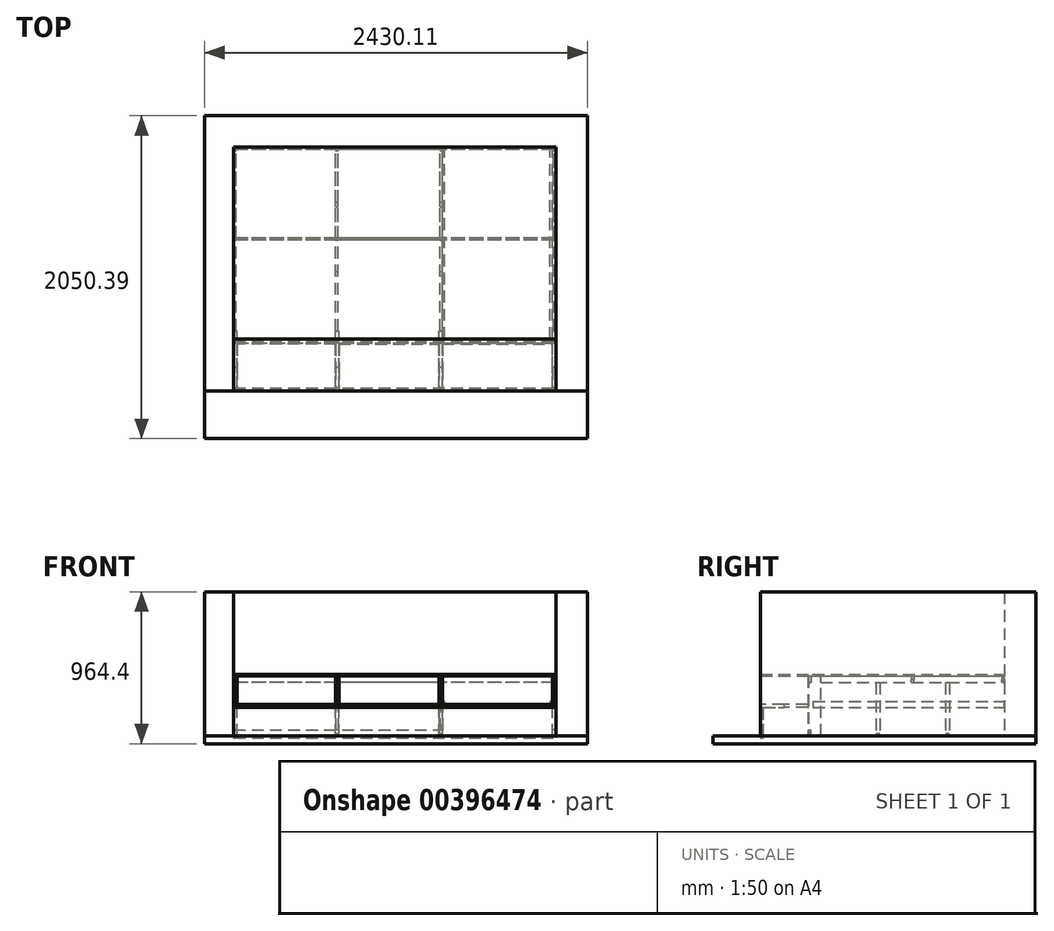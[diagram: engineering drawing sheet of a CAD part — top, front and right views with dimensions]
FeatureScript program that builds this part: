
annotation { "Feature Type Name" : "Feature", "Feature Type Description" : "" }
export const myFeature = defineFeature(function(context is Context, id is Id, definition is map)
    precondition{}
    {
        {
            var Q0;
            Q0=qCreatedBy(makeId("Top.planeOp"),FACE);
            cPlane(context, id + "F0", {"entities" : qUnion([Q0]), "cplaneType" : CPlaneType.OFFSET, "offset" : 180 * mm, "width" : 150 * mm, "height" : 150 * mm});
        }
        {
            var Q0;
            Q0=qCreatedBy(id+"F0.planeOp",FACE);
            var sketch = newSketch(context, id + "F1", { "sketchPlane" : qUnion([Q0])});
            skLineSegment(sketch, "E0.bottom", {"start": v(0, 0) * mm, "end": v(-2045, 0) * mm});
            skLineSegment(sketch, "E0.top", {"start": v(-20, 300) * mm, "end": v(-720, 300) * mm});
            skLineSegment(sketch, "E0.left", {"start": v(0, 0) * mm, "end": v(0, 150) * mm});
            skLineSegment(sketch, "E0.right", {"start": v(-2045, 0) * mm, "end": v(-2045, 150) * mm});
            skLineSegment(sketch, "E1.top", {"start": v(-2045, 150) * mm, "end": v(-2025, 150) * mm});
            skLineSegment(sketch, "E1.right", {"start": v(-2025, 300) * mm, "end": v(-2025, 150) * mm});
            skLineSegment(sketch, "E2.top", {"start": v(-1377.5, 150) * mm, "end": v(-1397.5, 150) * mm});
            skLineSegment(sketch, "E2.left", {"start": v(-1377.5, 300) * mm, "end": v(-1377.5, 150) * mm});
            skLineSegment(sketch, "E2.right", {"start": v(-1397.5, 300) * mm, "end": v(-1397.5, 150) * mm});
            skLineSegment(sketch, "E3.top", {"start": v(-720, 150) * mm, "end": v(-740, 150) * mm});
            skLineSegment(sketch, "E3.left", {"start": v(-720, 300) * mm, "end": v(-720, 150) * mm});
            skLineSegment(sketch, "E3.right", {"start": v(-740, 300) * mm, "end": v(-740, 150) * mm});
            skLineSegment(sketch, "E4.top", {"start": v(0, 150) * mm, "end": v(-20, 150) * mm});
            skLineSegment(sketch, "E5.trimOffspring", {"start": v(-1397.5, 300) * mm, "end": v(-2025, 300) * mm});
            skLineSegment(sketch, "E6.trimOffspring", {"start": v(-740, 300) * mm, "end": v(-1377.5, 300) * mm});
            skLineSegment(sketch, "E7", {"start": v(-20, 150) * mm, "end": v(-20, 300) * mm});
            skSolve(sketch);
        }
        {
            var Q0;
            Q0=makeQuery(id+"F1.imprint","IMPRINT",FACE,{"disambiguationData":[TD([[makeQuery(id+"F1.imprint","IMPRINT",EDGE,{"derivedFrom":sQuery(id+"F1.wireOp",EDGE,"E0.bottom")}),-1.0]])]});
            extrude(context, id + "F2", {"entities" : qUnion([Q0]), "depth" : 20 * mm});
        }
        {
            var Q0;
            Q0=makeQuery(id+"F2.opExtrude","SWEPT_FACE",FACE,{"disambiguationData":[OSD([sQuery(id+"F1.wireOp",EDGE,"E7")])]});
            var sketch = newSketch(context, id + "F3", { "sketchPlane" : qUnion([Q0])});
            skLineSegment(sketch, "E8.bottom", {"start": v(20, 0) * mm, "end": v(305, 0) * mm});
            skLineSegment(sketch, "E8.top", {"start": v(0, 380) * mm, "end": v(305, 380) * mm});
            skLineSegment(sketch, "E8.right", {"start": v(383.3, 0) * mm, "end": v(383.3, 380) * mm});
            skLineSegment(sketch, "E9.0.0", {"start": v(20, 180) * mm, "end": v(150, 180) * mm});
            skLineSegment(sketch, "E9.0.1", {"start": v(150, 180) * mm, "end": v(150, 200) * mm});
            skLineSegment(sketch, "E9.0.2", {"start": v(150, 200) * mm, "end": v(0, 200) * mm});
            skLineSegment(sketch, "E10.trimOffspring", {"start": v(0, 200) * mm, "end": v(0, 380) * mm});
            skLineSegment(sketch, "E11.top", {"start": v(305, 340) * mm, "end": v(320, 340) * mm});
            skLineSegment(sketch, "E11.left", {"start": v(305, 380) * mm, "end": v(305, 340) * mm});
            skLineSegment(sketch, "E11.right", {"start": v(320, 380) * mm, "end": v(320, 340) * mm});
            skLineSegment(sketch, "E12.top", {"start": v(305, 40) * mm, "end": v(320, 40) * mm});
            skLineSegment(sketch, "E12.left", {"start": v(305, 0) * mm, "end": v(305, 40) * mm});
            skLineSegment(sketch, "E12.right", {"start": v(320, 0) * mm, "end": v(320, 40) * mm});
            skLineSegment(sketch, "E13.0", {"start": v(20, 0) * mm, "end": v(20, 180) * mm});
            skPoint(sketch, "E14.orphan", {"position": v(0, 180) * mm});
            skLineSegment(sketch, "E15.trimOffspring", {"start": v(320, 380) * mm, "end": v(383.3, 380) * mm});
            skLineSegment(sketch, "E16.trimOffspring", {"start": v(320, 0) * mm, "end": v(383.3, 0) * mm});
            skSolve(sketch);
        }
        {
            var Q0;
            Q0=makeQuery(id+"F3.imprint","IMPRINT",FACE,{"disambiguationData":[TD([[makeQuery(id+"F3.imprint","IMPRINT",EDGE,{"derivedFrom":sQuery(id+"F3.wireOp",EDGE,"E8.bottom")}),1.0]])]});
            var Q1;
            Q1=makeQuery(id+"F3.imprint","IMPRINT",FACE,{"disambiguationData":[TD([[makeQuery(id+"F3.imprint","IMPRINT",EDGE,{"derivedFrom":sQuery(id+"F3.wireOp",EDGE,"E9.0.1")}),1.0]])]});
            extrude(context, id + "F4", {"entities" : qUnion([Q0, Q1]), "depth" : 20 * mm});
        }
        {
            var Q0;
            Q0=makeQuery(id+"F4.opExtrude","SWEPT_BODY",BODY,{"disambiguationData":[OSD([sQuery(id+"F3.wireOp",EDGE,"E8.bottom"),sQuery(id+"F3.wireOp",EDGE,"E8.top"),sQuery(id+"F3.wireOp",EDGE,"E8.left"),sQuery(id+"F3.wireOp",EDGE,"E8.right"),sQuery(id+"F3.wireOp",EDGE,"E9.0.0"),sQuery(id+"F3.wireOp",EDGE,"E9.0.1"),sQuery(id+"F3.wireOp",EDGE,"E9.0.2"),sQuery(id+"F3.wireOp",EDGE,"E10.trimOffspring")])]});
            transform(context, id + "F5", {"entities" : qUnion([Q0]), "transformType" : TransformType.TRANSLATION_3D, "dx" : -720 * mm, "dy" : 0 * mm, "dz" : 0 * mm, "makeCopy" : true});
        }
        {
            var Q0;
            Q0=makeQuery(id+"F5.opPattern","COPY",BODY,{"derivedFrom":makeQuery(id+"F4.opExtrude","SWEPT_BODY",BODY,{"disambiguationData":[OSD([sQuery(id+"F3.wireOp",EDGE,"E8.bottom"),sQuery(id+"F3.wireOp",EDGE,"E8.top"),sQuery(id+"F3.wireOp",EDGE,"E8.left"),sQuery(id+"F3.wireOp",EDGE,"E8.right"),sQuery(id+"F3.wireOp",EDGE,"E9.0.0"),sQuery(id+"F3.wireOp",EDGE,"E9.0.1"),sQuery(id+"F3.wireOp",EDGE,"E9.0.2"),sQuery(id+"F3.wireOp",EDGE,"E10.trimOffspring")])]}),"instanceName":"1"});
            transform(context, id + "F6", {"entities" : qUnion([Q0]), "transformType" : TransformType.TRANSLATION_3D, "dx" : -657.5 * mm, "dy" : 0 * mm, "dz" : 0 * mm, "makeCopy" : true});
        }
        {
            var Q0;
            Q0=makeQuery(id+"F6.opPattern","COPY",BODY,{"derivedFrom":makeQuery(id+"F5.opPattern","COPY",BODY,{"derivedFrom":makeQuery(id+"F4.opExtrude","SWEPT_BODY",BODY,{"disambiguationData":[OSD([sQuery(id+"F3.wireOp",EDGE,"E8.bottom"),sQuery(id+"F3.wireOp",EDGE,"E8.top"),sQuery(id+"F3.wireOp",EDGE,"E8.left"),sQuery(id+"F3.wireOp",EDGE,"E8.right"),sQuery(id+"F3.wireOp",EDGE,"E9.0.0"),sQuery(id+"F3.wireOp",EDGE,"E9.0.1"),sQuery(id+"F3.wireOp",EDGE,"E9.0.2"),sQuery(id+"F3.wireOp",EDGE,"E10.trimOffspring")])]}),"instanceName":"1"}),"instanceName":"1"});
            transform(context, id + "F7", {"entities" : qUnion([Q0]), "transformType" : TransformType.TRANSLATION_3D, "dx" : -647.5 * mm, "dy" : 0 * mm, "dz" : 0 * mm, "makeCopy" : true});
        }
        {
            var Q0;
            Q0=qCreatedBy(makeId("Top.planeOp"),FACE);
            var sketch = newSketch(context, id + "F8", { "sketchPlane" : qUnion([Q0])});
            skPoint(sketch, "E17.0", {"position": v(-2045, 320) * mm});
            skPoint(sketch, "E18.0", {"position": v(-720, 305) * mm});
            skLineSegment(sketch, "E19.bottom", {"start": v(-2045, 320) * mm, "end": v(-720, 320) * mm});
            skLineSegment(sketch, "E19.top", {"start": v(-2045, 305) * mm, "end": v(-720, 305) * mm});
            skLineSegment(sketch, "E19.right", {"start": v(-720, 320) * mm, "end": v(-720, 305) * mm});
            skLineSegment(sketch, "E20", {"start": v(-2045, 320) * mm, "end": v(-2045, 305) * mm});
            skSolve(sketch);
        }
        {
            var Q0;
            Q0 = qSketchRegion(id + "F8", true);
            extrude(context, id + "F9", {"entities" : qUnion([Q0]), "depth" : 40 * mm});
        }
        {
            var Q0;
            Q0=makeQuery(id+"F4.opExtrude","CAP_FACE",FACE,{"disambiguationData":[OSD([sQuery(id+"F3.wireOp",EDGE,"E8.bottom"),sQuery(id+"F3.wireOp",EDGE,"E8.top"),sQuery(id+"F3.wireOp",EDGE,"E8.left"),sQuery(id+"F3.wireOp",EDGE,"E8.right"),sQuery(id+"F3.wireOp",EDGE,"E9.0.0"),sQuery(id+"F3.wireOp",EDGE,"E9.0.1"),sQuery(id+"F3.wireOp",EDGE,"E9.0.2"),sQuery(id+"F3.wireOp",EDGE,"E10.trimOffspring"),sQuery(id+"F3.wireOp",EDGE,"E11.top"),sQuery(id+"F3.wireOp",EDGE,"E11.left"),sQuery(id+"F3.wireOp",EDGE,"E11.right"),sQuery(id+"F3.wireOp",EDGE,"E12.top"),sQuery(id+"F3.wireOp",EDGE,"E12.left"),sQuery(id+"F3.wireOp",EDGE,"E12.right")])],"isStart":false});
            var sketch = newSketch(context, id + "F10", { "sketchPlane" : qUnion([Q0])});
            skLineSegment(sketch, "E21.bottom", {"start": v(383.3, 380) * mm, "end": v(959.15, 380) * mm});
            skLineSegment(sketch, "E21.top", {"start": v(383.3, 340) * mm, "end": v(1530, 340) * mm});
            skLineSegment(sketch, "E21.right", {"start": v(1550, 380) * mm, "end": v(1550, 360) * mm});
            skLineSegment(sketch, "E22.0", {"start": v(974.15, 380) * mm, "end": v(974.15, 360) * mm});
            skLineSegment(sketch, "E23.0", {"start": v(959.15, 380) * mm, "end": v(959.15, 360) * mm});
            skLineSegment(sketch, "E24.trimOffspring", {"start": v(974.15, 380) * mm, "end": v(1550, 380) * mm});
            skLineSegment(sketch, "E25", {"start": v(974.15, 360) * mm, "end": v(959.15, 360) * mm});
            skLineSegment(sketch, "E26", {"start": v(1550, 360) * mm, "end": v(1530, 360) * mm});
            skLineSegment(sketch, "E27", {"start": v(1530, 360) * mm, "end": v(1530, 340) * mm});
            skLineSegment(sketch, "E28", {"start": v(383.3, 380) * mm, "end": v(383.3, 340) * mm});
            skSolve(sketch);
        }
        {
            var Q0;
            Q0 = qSketchRegion(id + "F10", true);
            extrude(context, id + "F11", {"entities" : qUnion([Q0]), "oppositeDirection" : true, "depth" : 15 * mm});
        }
        {
            var Q0;
            Q0=makeQuery(id+"F11.opExtrude","SWEPT_BODY",BODY,{"disambiguationData":[OSD([sQuery(id+"F10.wireOp",EDGE,"E21.bottom"),sQuery(id+"F10.wireOp",EDGE,"E21.top"),sQuery(id+"F10.wireOp",EDGE,"E21.left"),sQuery(id+"F10.wireOp",EDGE,"E21.right"),sQuery(id+"F10.wireOp",EDGE,"E22.0"),sQuery(id+"F10.wireOp",EDGE,"E23.0"),sQuery(id+"F10.wireOp",EDGE,"E24.trimOffspring"),sQuery(id+"F10.wireOp",EDGE,"E25"),sQuery(id+"F10.wireOp",EDGE,"E26"),sQuery(id+"F10.wireOp",EDGE,"sHKAyeEh-goYe-EqED-aYtI-0ct1l86yUGji")])]});
            transform(context, id + "F12", {"entities" : qUnion([Q0]), "transformType" : TransformType.TRANSLATION_3D, "dx" : -2030 * mm, "dy" : 0 * mm, "dz" : 0 * mm, "makeCopy" : true});
        }
        {
            var Q0;
            Q0=makeQuery(id+"F11.opExtrude","SWEPT_BODY",BODY,{"disambiguationData":[OSD([sQuery(id+"F10.wireOp",EDGE,"E21.bottom"),sQuery(id+"F10.wireOp",EDGE,"E21.top"),sQuery(id+"F10.wireOp",EDGE,"E21.left"),sQuery(id+"F10.wireOp",EDGE,"E21.right"),sQuery(id+"F10.wireOp",EDGE,"E22.0"),sQuery(id+"F10.wireOp",EDGE,"E23.0"),sQuery(id+"F10.wireOp",EDGE,"E24.trimOffspring"),sQuery(id+"F10.wireOp",EDGE,"E25"),sQuery(id+"F10.wireOp",EDGE,"E26"),sQuery(id+"F10.wireOp",EDGE,"sHKAyeEh-goYe-EqED-aYtI-0ct1l86yUGji")])]});
            transform(context, id + "F13", {"entities" : qUnion([Q0]), "transformType" : TransformType.TRANSLATION_3D, "dx" : -720 * mm, "dy" : 0 * mm, "dz" : 0 * mm, "makeCopy" : true});
        }
        {
            var Q0;
            Q0=makeQuery(id+"F13.opPattern","COPY",BODY,{"derivedFrom":makeQuery(id+"F11.opExtrude","SWEPT_BODY",BODY,{"disambiguationData":[OSD([sQuery(id+"F10.wireOp",EDGE,"E21.bottom"),sQuery(id+"F10.wireOp",EDGE,"E21.top"),sQuery(id+"F10.wireOp",EDGE,"E21.left"),sQuery(id+"F10.wireOp",EDGE,"E21.right"),sQuery(id+"F10.wireOp",EDGE,"E22.0"),sQuery(id+"F10.wireOp",EDGE,"E23.0"),sQuery(id+"F10.wireOp",EDGE,"E24.trimOffspring"),sQuery(id+"F10.wireOp",EDGE,"E25"),sQuery(id+"F10.wireOp",EDGE,"E26"),sQuery(id+"F10.wireOp",EDGE,"sHKAyeEh-goYe-EqED-aYtI-0ct1l86yUGji")])]}),"instanceName":"1"});
            transform(context, id + "F14", {"entities" : qUnion([Q0]), "transformType" : TransformType.TRANSLATION_3D, "dx" : -662.5 * mm, "dy" : 0 * mm, "dz" : 0 * mm, "makeCopy" : true});
        }
        {
            var Q0;
            Q0=makeQuery(id+"F11.opExtrude","SWEPT_FACE",FACE,{"disambiguationData":[OSD([sQuery(id+"F10.wireOp",EDGE,"E21.right")])]});
            var sketch = newSketch(context, id + "F15", { "sketchPlane" : qUnion([Q0])});
            skLineSegment(sketch, "E29.bottom", {"start": v(15, 380) * mm, "end": v(720, 380) * mm});
            skLineSegment(sketch, "E29.top", {"start": v(0, 340) * mm, "end": v(2045, 340) * mm});
            skLineSegment(sketch, "E29.left", {"start": v(0, 360) * mm, "end": v(0, 340) * mm});
            skLineSegment(sketch, "E30", {"start": v(2045, 340) * mm, "end": v(2045, 360) * mm});
            skPoint(sketch, "E31.0", {"position": v(2030, 360) * mm});
            skLineSegment(sketch, "E32", {"start": v(2045, 360) * mm, "end": v(2030, 360) * mm});
            skLineSegment(sketch, "E33", {"start": v(2030, 360) * mm, "end": v(2030, 380) * mm});
            skPoint(sketch, "E34.orphan", {"position": v(2045, 380) * mm});
            skPoint(sketch, "E35.0", {"position": v(1397.5, 360) * mm});
            skPoint(sketch, "E36.0", {"position": v(1382.5, 360) * mm});
            skLineSegment(sketch, "E37", {"start": v(1382.5, 380) * mm, "end": v(1382.5, 360) * mm});
            skLineSegment(sketch, "E38", {"start": v(1397.5, 360) * mm, "end": v(1397.5, 380) * mm});
            skLineSegment(sketch, "E39.trimOffspring", {"start": v(1397.5, 380) * mm, "end": v(2030, 380) * mm});
            skLineSegment(sketch, "E40", {"start": v(1382.5, 360) * mm, "end": v(1397.5, 360) * mm});
            skPoint(sketch, "E41.0", {"position": v(735, 360) * mm});
            skPoint(sketch, "E42.0", {"position": v(720, 380) * mm});
            skLineSegment(sketch, "E43.bottom", {"start": v(735, 360) * mm, "end": v(720, 360) * mm});
            skLineSegment(sketch, "E43.left", {"start": v(735, 360) * mm, "end": v(735, 380) * mm});
            skLineSegment(sketch, "E43.right", {"start": v(720, 360) * mm, "end": v(720, 380) * mm});
            skLineSegment(sketch, "E44.trimOffspring", {"start": v(735, 380) * mm, "end": v(1382.5, 380) * mm});
            skPoint(sketch, "E45.0", {"position": v(15, 360) * mm});
            skLineSegment(sketch, "E46.bottom", {"start": v(15, 360) * mm, "end": v(0, 360) * mm});
            skLineSegment(sketch, "E46.left", {"start": v(15, 360) * mm, "end": v(15, 380) * mm});
            skPoint(sketch, "E46.top.end.orphan", {"position": v(0, 380) * mm});
            skSolve(sketch);
        }
        {
            var Q0;
            Q0=makeQuery(id+"F15.imprint","IMPRINT",FACE,{"disambiguationData":[TD([[makeQuery(id+"F15.imprint","IMPRINT",EDGE,{"derivedFrom":sQuery(id+"F15.wireOp",EDGE,"E29.bottom")}),-1.0]])]});
            extrude(context, id + "F16", {"entities" : qUnion([Q0]), "oppositeDirection" : true, "depth" : 15 * mm});
        }
        {
            var Q0;
            Q0=makeQuery(id+"F13.opPattern","COPY",FACE,{"derivedFrom":makeQuery(id+"F11.opExtrude","CAP_FACE",FACE,{"disambiguationData":[OSD([sQuery(id+"F10.wireOp",EDGE,"E21.bottom"),sQuery(id+"F10.wireOp",EDGE,"E21.top"),sQuery(id+"F10.wireOp",EDGE,"E21.left"),sQuery(id+"F10.wireOp",EDGE,"E21.right"),sQuery(id+"F10.wireOp",EDGE,"E22.0"),sQuery(id+"F10.wireOp",EDGE,"E23.0"),sQuery(id+"F10.wireOp",EDGE,"E24.trimOffspring"),sQuery(id+"F10.wireOp",EDGE,"E25"),sQuery(id+"F10.wireOp",EDGE,"E26"),sQuery(id+"F10.wireOp",EDGE,"E27")])],"isStart":true}),"instanceName":"1"});
            var sketch = newSketch(context, id + "F17", { "sketchPlane" : qUnion([Q0])});
            skLineSegment(sketch, "E47.0", {"start": v(733.3, 340) * mm, "end": v(733.3, 15) * mm});
            skLineSegment(sketch, "E48.0", {"start": v(760, 340) * mm, "end": v(760, 15) * mm});
            skLineSegment(sketch, "E49", {"start": v(733.3, 340) * mm, "end": v(760, 340) * mm});
            skLineSegment(sketch, "E50", {"start": v(733.3, 15) * mm, "end": v(760, 15) * mm});
            skPoint(sketch, "E51.0", {"position": v(20, 0) * mm});
            skSolve(sketch);
        }
        {
            var Q0;
            Q0=makeQuery(id+"F17.imprint","IMPRINT",FACE,{"disambiguationData":[TD([[makeQuery(id+"F17.imprint","IMPRINT",EDGE,{"derivedFrom":sQuery(id+"F17.wireOp",EDGE,"E47.0")}),1.0]])]});
            extrude(context, id + "F18", {"entities" : qUnion([Q0]), "oppositeDirection" : true, "depth" : 15 * mm});
        }
        {
            var Q0;
            Q0=makeQuery(id+"F18.opExtrude","SWEPT_BODY",BODY,{"disambiguationData":[OSD([sQuery(id+"F17.wireOp",EDGE,"E47.0"),sQuery(id+"F17.wireOp",EDGE,"E48.0"),sQuery(id+"F17.wireOp",EDGE,"E49"),sQuery(id+"F17.wireOp",EDGE,"E50")])]});
            transform(context, id + "F19", {"entities" : qUnion([Q0]), "transformType" : TransformType.TRANSLATION_3D, "dx" : 0 * mm, "dy" : 440 * mm, "dz" : 0 * mm, "makeCopy" : true});
        }
        {
            var Q0;
            Q0=makeQuery(id+"F18.opExtrude","SWEPT_BODY",BODY,{"disambiguationData":[OSD([sQuery(id+"F17.wireOp",EDGE,"E47.0"),sQuery(id+"F17.wireOp",EDGE,"E48.0"),sQuery(id+"F17.wireOp",EDGE,"E49"),sQuery(id+"F17.wireOp",EDGE,"E50")])]});
            transform(context, id + "F20", {"entities" : qUnion([Q0]), "transformType" : TransformType.TRANSLATION_3D, "dx" : -662.5 * mm, "dy" : 0 * mm, "dz" : 0 * mm, "makeCopy" : true});
        }
        {
            var Q0;
            Q0=makeQuery(id+"F19.opPattern","COPY",BODY,{"derivedFrom":makeQuery(id+"F18.opExtrude","SWEPT_BODY",BODY,{"disambiguationData":[OSD([sQuery(id+"F17.wireOp",EDGE,"E47.0"),sQuery(id+"F17.wireOp",EDGE,"E48.0"),sQuery(id+"F17.wireOp",EDGE,"E49"),sQuery(id+"F17.wireOp",EDGE,"E50")])]}),"instanceName":"1"});
            transform(context, id + "F21", {"entities" : qUnion([Q0]), "transformType" : TransformType.TRANSLATION_3D, "dx" : -662.5 * mm, "dy" : 0 * mm, "dz" : 0 * mm, "makeCopy" : true});
        }
        {
            var Q0;
            Q0=makeQuery(id+"F5.opPattern","COPY",FACE,{"derivedFrom":makeQuery(id+"F4.opExtrude","CAP_FACE",FACE,{"disambiguationData":[OSD([sQuery(id+"F3.wireOp",EDGE,"E8.bottom"),sQuery(id+"F3.wireOp",EDGE,"E8.top"),sQuery(id+"F3.wireOp",EDGE,"E8.left"),sQuery(id+"F3.wireOp",EDGE,"E8.right"),sQuery(id+"F3.wireOp",EDGE,"E9.0.0"),sQuery(id+"F3.wireOp",EDGE,"E9.0.1"),sQuery(id+"F3.wireOp",EDGE,"E9.0.2"),sQuery(id+"F3.wireOp",EDGE,"E10.trimOffspring"),sQuery(id+"F3.wireOp",EDGE,"E11.top"),sQuery(id+"F3.wireOp",EDGE,"E11.left"),sQuery(id+"F3.wireOp",EDGE,"E11.right"),sQuery(id+"F3.wireOp",EDGE,"E12.top"),sQuery(id+"F3.wireOp",EDGE,"E12.left"),sQuery(id+"F3.wireOp",EDGE,"E12.right")])],"isStart":false}),"instanceName":"1"});
            var sketch = newSketch(context, id + "F22", { "sketchPlane" : qUnion([Q0])});
            skPoint(sketch, "E52.0", {"position": v(1550, 340) * mm});
            skLineSegment(sketch, "E53.bottom", {"start": v(333.3, 180) * mm, "end": v(1550, 180) * mm});
            skLineSegment(sketch, "E53.top", {"start": v(333.3, 220) * mm, "end": v(1550, 220) * mm});
            skLineSegment(sketch, "E53.right", {"start": v(1550, 180) * mm, "end": v(1550, 220) * mm});
            skLineSegment(sketch, "E54", {"start": v(333.3, 220) * mm, "end": v(333.3, 180) * mm});
            skSolve(sketch);
        }
        {
            var Q0;
            Q0=makeQuery(id+"F22.imprint","IMPRINT",FACE,{"disambiguationData":[TD([[makeQuery(id+"F22.imprint","IMPRINT",EDGE,{"derivedFrom":sQuery(id+"F22.wireOp",EDGE,"E53.bottom")}),1.0]])]});
            extrude(context, id + "F23", {"entities" : qUnion([Q0]), "depth" : 15 * mm});
        }
        {
            var Q0;
            Q0=makeQuery(id+"F23.opExtrude","SWEPT_BODY",BODY,{"disambiguationData":[OSD([sQuery(id+"F22.wireOp",EDGE,"E53.bottom"),sQuery(id+"F22.wireOp",EDGE,"E53.top"),sQuery(id+"F22.wireOp",EDGE,"E53.right"),sQuery(id+"F22.wireOp",EDGE,"E54")])]});
            transform(context, id + "F24", {"entities" : qUnion([Q0]), "transformType" : TransformType.TRANSLATION_3D, "dx" : (700 - 15) * mm, "dy" : 0 * mm, "dz" : 0 * mm, "makeCopy" : true});
        }
        {
            var Q0;
            Q0=qCreatedBy(makeId("Top.planeOp"),FACE);
            var sketch = newSketch(context, id + "F25", { "sketchPlane" : qUnion([Q0])});
            skPoint(sketch, "E55.0", {"position": v(0, 1550) * mm});
            skPoint(sketch, "E56.0", {"position": v(-2045, 1550) * mm});
            skPoint(sketch, "E57.0", {"position": v(-2045, 0) * mm});
            skLineSegment(sketch, "E58.bottom", {"start": v(0, 0) * mm, "end": v(200, 0) * mm});
            skLineSegment(sketch, "E58.left", {"start": v(0, 0) * mm, "end": v(0, 1550) * mm});
            skLineSegment(sketch, "E58.right", {"start": v(200, 0) * mm, "end": v(200, 1750) * mm});
            skLineSegment(sketch, "E59.bottom", {"start": v(0, 1550) * mm, "end": v(-2045, 1550) * mm});
            skLineSegment(sketch, "E59.top", {"start": v(200, 1750) * mm, "end": v(-2230.11, 1750) * mm});
            skLineSegment(sketch, "E60.bottom", {"start": v(-2045, 0) * mm, "end": v(-2230.11, 0) * mm});
            skLineSegment(sketch, "E60.left", {"start": v(-2045, 0) * mm, "end": v(-2045, 1550) * mm});
            skLineSegment(sketch, "E60.right", {"start": v(-2230.11, 0) * mm, "end": v(-2230.11, 1750) * mm});
            skLineSegment(sketch, "E61.bottom", {"start": v(-2230.11, 0) * mm, "end": v(200, 0) * mm});
            skLineSegment(sketch, "E61.top", {"start": v(-2230.11, -300.39) * mm, "end": v(200, -300.39) * mm});
            skLineSegment(sketch, "E61.left", {"start": v(-2230.11, 0) * mm, "end": v(-2230.11, -300.39) * mm});
            skLineSegment(sketch, "E61.right", {"start": v(200, 0) * mm, "end": v(200, -300.39) * mm});
            skSolve(sketch);
        }
        {
            var Q0;
            {var subQ1=sQuery(id+"F25.wireOp",EDGE,"E58.left");Q0=makeQuery(id+"F25.imprint","IMPRINT",FACE,{"disambiguationData":[TD([[makeQuery(id+"F25.imprint","IMPRINT",EDGE,{"derivedFrom":subQ1}),-1.0]])]});}
            extrude(context, id + "F26", {"entities" : qUnion([Q0]), "depth" : 914.4 * mm});
        }
        {
            var Q0;
            Q0=makeQuery(id+"F25.imprint","IMPRINT",FACE,{"disambiguationData":[TD([[makeQuery(id+"F25.imprint","IMPRINT",EDGE,{"derivedFrom":sQuery(id+"F25.wireOp",EDGE,"E61.top")}),1.0]])]});
            var Q1;
            {var subQ0=sQuery(id+"F25.wireOp",EDGE,"E58.left");Q1=makeQuery(id+"F25.imprint","IMPRINT",FACE,{"disambiguationData":[TD([[makeQuery(id+"F25.imprint","IMPRINT",EDGE,{"derivedFrom":subQ0}),1.0]])]});}
            var Q2;
            {var subQ1=sQuery(id+"F25.wireOp",EDGE,"E58.left");Q2=makeQuery(id+"F25.imprint","IMPRINT",FACE,{"disambiguationData":[TD([[makeQuery(id+"F25.imprint","IMPRINT",EDGE,{"derivedFrom":subQ1}),-1.0]])]});}
            extrude(context, id + "F27", {"entities" : qUnion([Q0, Q1, Q2]), "oppositeDirection" : true, "depth" : 50 * mm});
        }
        {
            var Q0;
            Q0=makeQuery(id+"F4.opExtrude","CAP_FACE",FACE,{"disambiguationData":[OSD([sQuery(id+"F3.wireOp",EDGE,"E8.bottom"),sQuery(id+"F3.wireOp",EDGE,"E8.top"),sQuery(id+"F3.wireOp",EDGE,"E8.right"),sQuery(id+"F3.wireOp",EDGE,"E9.0.0"),sQuery(id+"F3.wireOp",EDGE,"E9.0.1"),sQuery(id+"F3.wireOp",EDGE,"E9.0.2"),sQuery(id+"F3.wireOp",EDGE,"E10.trimOffspring"),sQuery(id+"F3.wireOp",EDGE,"E11.top"),sQuery(id+"F3.wireOp",EDGE,"E11.left"),sQuery(id+"F3.wireOp",EDGE,"E11.right"),sQuery(id+"F3.wireOp",EDGE,"E12.top"),sQuery(id+"F3.wireOp",EDGE,"E12.left"),sQuery(id+"F3.wireOp",EDGE,"E12.right"),sQuery(id+"F3.wireOp",EDGE,"E13.0"),sQuery(id+"F3.wireOp",EDGE,"E15.trimOffspring"),sQuery(id+"F3.wireOp",EDGE,"E16.trimOffspring")])],"isStart":false});
            var sketch = newSketch(context, id + "F28", { "sketchPlane" : qUnion([Q0])});
            skLineSegment(sketch, "E62.bottom", {"start": v(305, 380) * mm, "end": v(320, 380) * mm});
            skLineSegment(sketch, "E62.top", {"start": v(305, 340) * mm, "end": v(320, 340) * mm});
            skLineSegment(sketch, "E62.left", {"start": v(305, 380) * mm, "end": v(305, 340) * mm});
            skLineSegment(sketch, "E62.right", {"start": v(320, 380) * mm, "end": v(320, 340) * mm});
            skSolve(sketch);
        }
        {
            var Q0;
            Q0 = qSketchRegion(id + "F28", true);
            extrude(context, id + "F29", {"entities" : qUnion([Q0]), "oppositeDirection" : true, "depth" : 2045 * mm});
        }
        {
            var Q0;
            Q0=makeQuery(id+"F29.opExtrude","SWEPT_FACE",FACE,{"disambiguationData":[OSD([sQuery(id+"F28.wireOp",EDGE,"E62.left")])]});
            var sketch = newSketch(context, id + "F30", { "sketchPlane" : qUnion([Q0])});
            skPoint(sketch, "E63.0", {"position": v(-2025, 380) * mm});
            skPoint(sketch, "E64.0", {"position": v(-1397.5, 0) * mm});
            skLineSegment(sketch, "E65.bottom", {"start": v(-2025, 380) * mm, "end": v(-1397.5, 380) * mm});
            skLineSegment(sketch, "E65.top", {"start": v(-2025, 0) * mm, "end": v(-1397.5, 0) * mm});
            skLineSegment(sketch, "E65.left", {"start": v(-2025, 380) * mm, "end": v(-2025, 0) * mm});
            skLineSegment(sketch, "E65.right", {"start": v(-1397.5, 380) * mm, "end": v(-1397.5, 0) * mm});
            skSolve(sketch);
        }
        {
            var Q0;
            Q0 = qSketchRegion(id + "F30", true);
            extrude(context, id + "F31", {"entities" : qUnion([Q0]), "depth" : 5 * mm});
        }
        {
            var Q0;
            Q0=makeQuery(id+"F29.opExtrude","SWEPT_FACE",FACE,{"disambiguationData":[OSD([sQuery(id+"F28.wireOp",EDGE,"E62.left")])]});
            var sketch = newSketch(context, id + "F32", { "sketchPlane" : qUnion([Q0])});
            skPoint(sketch, "E66.0", {"position": v(-1377.5, 380) * mm});
            skPoint(sketch, "E67.0", {"position": v(-740, 0) * mm});
            skLineSegment(sketch, "E68.bottom", {"start": v(-1377.5, 380) * mm, "end": v(-740, 380) * mm});
            skLineSegment(sketch, "E68.top", {"start": v(-1377.5, 0) * mm, "end": v(-740, 0) * mm});
            skLineSegment(sketch, "E68.left", {"start": v(-1377.5, 380) * mm, "end": v(-1377.5, 0) * mm});
            skLineSegment(sketch, "E68.right", {"start": v(-740, 380) * mm, "end": v(-740, 0) * mm});
            skSolve(sketch);
        }
        {
            var Q0;
            Q0 = qSketchRegion(id + "F32", true);
            extrude(context, id + "F33", {"entities" : qUnion([Q0]), "depth" : 5 * mm});
        }
        {
            var Q0;
            Q0=makeQuery(id+"F29.opExtrude","SWEPT_FACE",FACE,{"disambiguationData":[OSD([sQuery(id+"F28.wireOp",EDGE,"E62.left")])]});
            var sketch = newSketch(context, id + "F34", { "sketchPlane" : qUnion([Q0])});
            skPoint(sketch, "E69.0", {"position": v(-720, 380) * mm});
            skPoint(sketch, "E70.0", {"position": v(-20, 180) * mm});
            skLineSegment(sketch, "E71.bottom", {"start": v(-720, 380) * mm, "end": v(-20, 380) * mm});
            skLineSegment(sketch, "E71.top", {"start": v(-720, 180) * mm, "end": v(-20, 180) * mm});
            skLineSegment(sketch, "E71.left", {"start": v(-720, 380) * mm, "end": v(-720, 180) * mm});
            skLineSegment(sketch, "E71.right", {"start": v(-20, 380) * mm, "end": v(-20, 180) * mm});
            skSolve(sketch);
        }
        {
            var Q0;
            Q0 = qSketchRegion(id + "F34", true);
            extrude(context, id + "F35", {"entities" : qUnion([Q0]), "depth" : 5 * mm});
        }
        {
            var Q0;
            Q0=makeQuery(id+"F14.opPattern","COPY",FACE,{"derivedFrom":makeQuery(id+"F13.opPattern","COPY",FACE,{"derivedFrom":makeQuery(id+"F11.opExtrude","SWEPT_FACE",FACE,{"disambiguationData":[OSD([sQuery(id+"F10.wireOp",EDGE,"E22.0")])]}),"instanceName":"1"}),"instanceName":"1"});
            var sketch = newSketch(context, id + "F36", { "sketchPlane" : qUnion([Q0])});
            skLineSegment(sketch, "E72.bottom", {"start": v(-15, 340) * mm, "end": v(-720, 340) * mm});
            skLineSegment(sketch, "E72.top", {"start": v(0, 380) * mm, "end": v(-2045, 380) * mm});
            skLineSegment(sketch, "E72.left", {"start": v(0, 360) * mm, "end": v(0, 380) * mm});
            skLineSegment(sketch, "E72.right", {"start": v(-2045, 360) * mm, "end": v(-2045, 380) * mm});
            skLineSegment(sketch, "E73.top", {"start": v(-2030, 360) * mm, "end": v(-2045, 360) * mm});
            skLineSegment(sketch, "E73.left", {"start": v(-2030, 340) * mm, "end": v(-2030, 360) * mm});
            skLineSegment(sketch, "E74.bottom", {"start": v(-1382.5, 360) * mm, "end": v(-1397.5, 360) * mm});
            skLineSegment(sketch, "E74.left", {"start": v(-1382.5, 360) * mm, "end": v(-1382.5, 340) * mm});
            skLineSegment(sketch, "E74.right", {"start": v(-1397.5, 360) * mm, "end": v(-1397.5, 340) * mm});
            skLineSegment(sketch, "E75.bottom", {"start": v(-720, 360) * mm, "end": v(-735, 360) * mm});
            skLineSegment(sketch, "E75.left", {"start": v(-720, 360) * mm, "end": v(-720, 340) * mm});
            skLineSegment(sketch, "E75.right", {"start": v(-735, 360) * mm, "end": v(-735, 340) * mm});
            skLineSegment(sketch, "E76.top", {"start": v(-15, 360) * mm, "end": v(0, 360) * mm});
            skLineSegment(sketch, "E76.left", {"start": v(-15, 340) * mm, "end": v(-15, 360) * mm});
            skLineSegment(sketch, "E77.trimOffspring", {"start": v(-735, 340) * mm, "end": v(-1382.5, 340) * mm});
            skLineSegment(sketch, "E78.trimOffspring", {"start": v(-1397.5, 340) * mm, "end": v(-2030, 340) * mm});
            skSolve(sketch);
        }
        {
            var Q0;
            Q0 = qSketchRegion(id + "F36", true);
            extrude(context, id + "F37", {"entities" : qUnion([Q0]), "depth" : 15 * mm});
        }
        {
            var Q0;
            Q0=makeQuery(id+"F7.opPattern","COPY",FACE,{"derivedFrom":makeQuery(id+"F6.opPattern","COPY",FACE,{"derivedFrom":makeQuery(id+"F5.opPattern","COPY",FACE,{"derivedFrom":makeQuery(id+"F4.opExtrude","SWEPT_FACE",FACE,{"disambiguationData":[OSD([sQuery(id+"F3.wireOp",EDGE,"E8.top")])]}),"instanceName":"1"}),"instanceName":"1"}),"instanceName":"1"});
            var sketch = newSketch(context, id + "F38", { "sketchPlane" : qUnion([Q0])});
            skPoint(sketch, "E79.0", {"position": v(0, 1550) * mm});
            skPoint(sketch, "E80.0", {"position": v(-2045, 0) * mm});
            skLineSegment(sketch, "E81.bottom", {"start": v(-2045, 0) * mm, "end": v(0, 0) * mm});
            skLineSegment(sketch, "E81.top", {"start": v(-2045, 1550) * mm, "end": v(0, 1550) * mm});
            skLineSegment(sketch, "E81.left", {"start": v(-2045, 0) * mm, "end": v(-2045, 1550) * mm});
            skLineSegment(sketch, "E81.right", {"start": v(0, 0) * mm, "end": v(0, 1550) * mm});
            skLineSegment(sketch, "E82.0", {"start": v(-2045, 330.8) * mm, "end": v(0, 330.8) * mm});
            skSolve(sketch);
        }
        {
            var Q0;
            {var subQ0=sQuery(id+"F38.wireOp",EDGE,"E81.top");Q0=makeQuery(id+"F38.imprint","IMPRINT",FACE,{"disambiguationData":[TD([[makeQuery(id+"F38.imprint","IMPRINT",EDGE,{"derivedFrom":subQ0}),-1.0]])]});}
            extrude(context, id + "F39", {"entities" : qUnion([Q0]), "depth" : 10 * mm});
        }
        {
            var Q0;
            {var subQ3=sQuery(id+"F38.wireOp",EDGE,"E82.0");Q0=makeQuery(id+"F38.imprint","IMPRINT",FACE,{"disambiguationData":[TD([[makeQuery(id+"F38.imprint","IMPRINT",EDGE,{"derivedFrom":subQ3}),-1.0]])]});}
            var Q1;
            {var subQ3=sQuery(id+"F3.wireOp",EDGE,"E8.top");var subQ4=makeQuery(id+"F7.opPattern","COPY",EDGE,{"derivedFrom":makeQuery(id+"F6.opPattern","COPY",EDGE,{"derivedFrom":makeQuery(id+"F5.opPattern","COPY",EDGE,{"derivedFrom":makeQuery(id+"F4.opExtrude","CAP_EDGE",EDGE,{"disambiguationData":[OSD([subQ3])],"isStart":false}),"instanceName":"1"}),"instanceName":"1"}),"instanceName":"1"});Q1=makeQuery(id+"F38.imprint","IMPRINT",FACE,{"disambiguationData":[TD([[makeQuery(id+"F38.imprint","IMPRINT",EDGE,{"derivedFrom":subQ4}),1.0]])]});}
            extrude(context, id + "F40", {"entities" : qUnion([Q0, Q1]), "depth" : 10 * mm});
        }
        {
            var Q0;
            Q0=makeQuery(id+"F7.opPattern","COPY",FACE,{"derivedFrom":makeQuery(id+"F6.opPattern","COPY",FACE,{"derivedFrom":makeQuery(id+"F5.opPattern","COPY",FACE,{"derivedFrom":makeQuery(id+"F4.opExtrude","SWEPT_FACE",FACE,{"disambiguationData":[OSD([sQuery(id+"F3.wireOp",EDGE,"E13.0")])]}),"instanceName":"1"}),"instanceName":"1"}),"instanceName":"1"});
            var sketch = newSketch(context, id + "F41", { "sketchPlane" : qUnion([Q0])});
            skPoint(sketch, "E83.0", {"position": v(-2045, 180) * mm});
            skLineSegment(sketch, "E84.bottom", {"start": v(-2045, 180) * mm, "end": v(0, 180) * mm});
            skLineSegment(sketch, "E84.top", {"start": v(-2045, -13.26) * mm, "end": v(0, -13.26) * mm});
            skLineSegment(sketch, "E84.left", {"start": v(-2045, 180) * mm, "end": v(-2045, -13.26) * mm});
            skLineSegment(sketch, "E84.right", {"start": v(0, 180) * mm, "end": v(0, -13.26) * mm});
            skSolve(sketch);
        }
        {
            var Q0;
            Q0 = qSketchRegion(id + "F41", true);
            extrude(context, id + "F42", {"entities" : qUnion([Q0]), "depth" : 20 * mm});
        }
    });
